# Revit family: Reece_Tap_Dura_Mini Stop
name_source: partatom
category: Plumbing Fixtures
revit_build: Autodesk Revit 2018 (Build: 20181011_1500(x64)
units: mm (PartAtom-declared; Revit-internal decimal feet)

## family parameters
Cut with Voids When Loaded = No
Host = Face
Part Type = Normal
Room Calculation Point = Yes
Round Connector Dimension = Use Diameter
Shared = Yes

## types (1)
- Chrome
    CW Connection = No
    CWFU = 0
    Cost = 0 $
    Default Elevation = 0 mm  [stored 0 ft]
    Description = Dura Standard Mini Stop Chrome 15mm Lead Free
    Disclaimer = THIS FILE IS THE PROPERTY OF THE REECE GROUP. IT MAY NOT BE REPRODUCED, REVERSE-ENGINEERED, OR MODIFIED. ANY REPUBLICATION, TRANSMISSION, OR DISTRIBUTION FOR THE PURPOSE OF COMMERCIALLY EXPLOITING THE FILES IS PROHIBITED.
    HW Connection = No
    HWFU = 0
    Keynote = Product #15088, Reece_Tap_Dura_Mini Stop - Chrome
    Manufacturer = Dura
    Model = -
    Reece_Detail_Disclaimer = THIS FILE IS THE PROPERTY OF THE REECE GROUP. IT MAY NOT BE REPRODUCED, REVERSE-ENGINEERED, OR MODIFIED. ANY REPUBLICATION, TRANSMISSION, OR DISTRIBUTION FOR THE PURPOSE OF COMMERCIALLY EXPLOITING THE FILES IS PROHIBITED.
    Reece_Detail_Type = Mini Stop
    Reece_Material_Main = Reece_Brass_Chrome
    Reece_Overall_Height = 28 mm
    Reece_Product_Brand = Dura
    Reece_Product_Description = Dura Standard Mini Stop Chrome 15mm Lead Free
    Reece_Product_Mount = Wall Mounted
    Reece_Product_Number = 15088
    Reece_Product_Type = Tap
    Reece_Product_Web Page = https://www.reece.com.au
    Reece_Tap_Inlet = 13 mm  [stored 0.0426509 ft]
    Reece_Tap_Outlet = 13 mm  [stored 0.0426509 ft]
    Reece_Tap_Projection = 63 mm
    Type Comments = Tap
    URL = https://www.reece.com.au
    Vent Connection = No
    WFU = 0
    Waste Connection = No

note: [stored X ft] marks values corroborated as IEEE doubles in the binary element streams (Revit-internal decimal feet)

## geometry (parser evidence)
native form markers: Sweep x3
no freeform markers — native parametric forms only
